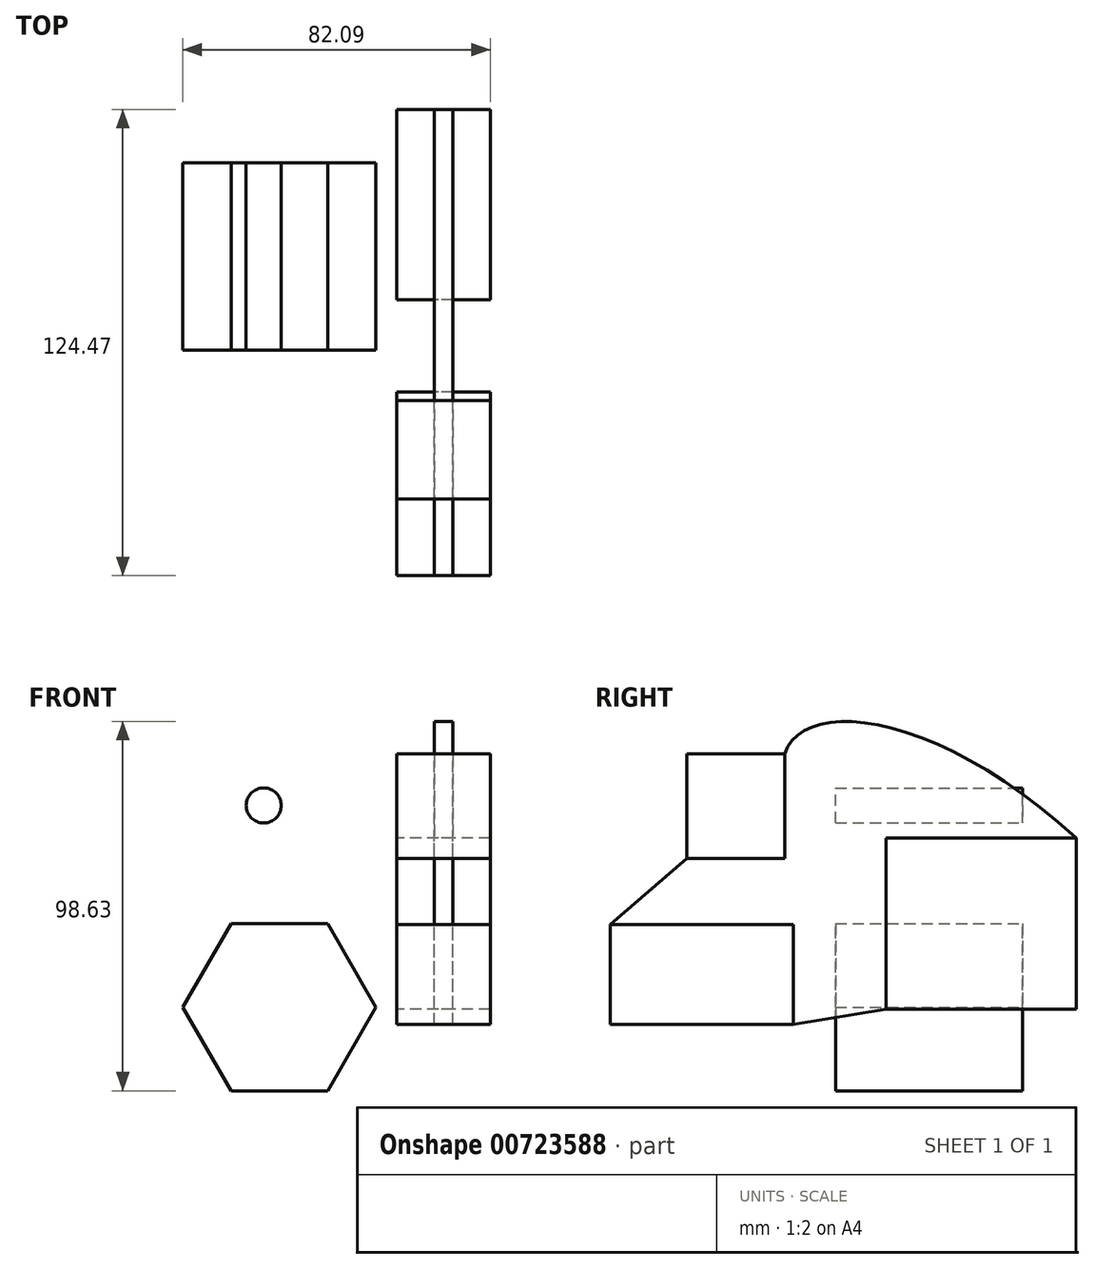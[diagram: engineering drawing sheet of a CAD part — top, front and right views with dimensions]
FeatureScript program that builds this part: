
annotation { "Feature Type Name" : "Feature", "Feature Type Description" : "" }
export const myFeature = defineFeature(function(context is Context, id is Id, definition is map)
    precondition{}
    {
        {
            var Q0;
            Q0=qCreatedBy(makeId("Right.planeOp"),FACE);
            var sketch = newSketch(context, id + "F0", { "sketchPlane" : qUnion([Q0])});
            skLineSegment(sketch, "E0.bottom", {"start": v(-64.75, 9.53) * mm, "end": v(-38.52, 9.53) * mm});
            skLineSegment(sketch, "E0.top", {"start": v(-64.75, 37.47) * mm, "end": v(-38.52, 37.47) * mm});
            skLineSegment(sketch, "E0.left", {"start": v(-64.75, 9.53) * mm, "end": v(-64.75, 37.47) * mm});
            skLineSegment(sketch, "E0.right", {"start": v(-38.52, 9.53) * mm, "end": v(-38.52, 37.47) * mm});
            skPoint(sketch, "E0.middle", {"position": v(-51.64, 23.5) * mm});
            skLineSegment(sketch, "E1.bottom", {"start": v(-36.2, -34.75) * mm, "end": v(-85.2, -34.75) * mm});
            skLineSegment(sketch, "E1.top", {"start": v(-36.2, -8.07) * mm, "end": v(-85.2, -8.07) * mm});
            skLineSegment(sketch, "E1.left", {"start": v(-36.2, -34.75) * mm, "end": v(-36.2, -8.07) * mm});
            skLineSegment(sketch, "E1.right", {"start": v(-85.2, -34.75) * mm, "end": v(-85.2, -8.07) * mm});
            skPoint(sketch, "E1.middle", {"position": v(-60.7, -21.41) * mm});
            skLineSegment(sketch, "E2.bottom", {"start": v(39.28, -30.76) * mm, "end": v(-11.52, -30.76) * mm});
            skLineSegment(sketch, "E2.top", {"start": v(39.28, 14.97) * mm, "end": v(-11.52, 14.97) * mm});
            skLineSegment(sketch, "E2.left", {"start": v(39.28, -30.76) * mm, "end": v(39.28, 14.97) * mm});
            skLineSegment(sketch, "E2.right", {"start": v(-11.52, -30.76) * mm, "end": v(-11.52, 14.97) * mm});
            skPoint(sketch, "E2.middle", {"position": v(13.88, -7.9) * mm});
            skLineSegment(sketch, "E3", {"start": v(-11.52, 14.97) * mm, "end": v(-38.52, 37.47) * mm});
            skLineSegment(sketch, "E4", {"start": v(-36.2, -34.75) * mm, "end": v(-11.52, -30.76) * mm});
            skLineSegment(sketch, "E5", {"start": v(-85.2, -8.07) * mm, "end": v(-64.75, 9.53) * mm});
            skFitSpline(sketch, "E6", {"points": [v(-38.52, 37.47) * mm, v(39.28, 14.97) * mm], "startDerivative": vector(14.54, 45.73) * mm, "endDerivative": vector(112.18, -102.88) * mm});
            skSolve(sketch);
        }
        {
            var Q0;
            Q0=makeQuery(id+"F0.imprint","IMPRINT",FACE,{"disambiguationData":[TD([[makeQuery(id+"F0.imprint","IMPRINT",EDGE,{"derivedFrom":sQuery(id+"F0.wireOp",EDGE,"E0.bottom")}),1.0]])]});
            var Q1;
            Q1=makeQuery(id+"F0.imprint","IMPRINT",FACE,{"disambiguationData":[TD([[makeQuery(id+"F0.imprint","IMPRINT",EDGE,{"derivedFrom":sQuery(id+"F0.wireOp",EDGE,"E2.bottom")}),-1.0]])]});
            var Q2;
            Q2=makeQuery(id+"F0.imprint","IMPRINT",FACE,{"disambiguationData":[TD([[makeQuery(id+"F0.imprint","IMPRINT",EDGE,{"derivedFrom":sQuery(id+"F0.wireOp",EDGE,"E1.bottom")}),-1.0]])]});
            extrude(context, id + "F1", {"entities" : qUnion([Q0, Q1, Q2]), "endBound" : BoundingType.SYMMETRIC, "depth" : 25 * mm, "offsetDistance" : 25 * mm});
        }
        {
            var Q0;
            Q0=makeQuery(id+"F0.imprint","IMPRINT",FACE,{"disambiguationData":[TD([[makeQuery(id+"F0.imprint","IMPRINT",EDGE,{"derivedFrom":sQuery(id+"F0.wireOp",EDGE,"E0.bottom")}),-1.0]])]});
            var Q1;
            Q1=makeQuery(id+"F0.imprint","IMPRINT",FACE,{"disambiguationData":[TD([[makeQuery(id+"F0.imprint","IMPRINT",EDGE,{"derivedFrom":sQuery(id+"F0.wireOp",EDGE,"E2.top")}),-1.0]])]});
            extrude(context, id + "F2", {"entities" : qUnion([Q0, Q1]), "endBound" : BoundingType.SYMMETRIC, "depth" : 5 * mm, "offsetDistance" : 25 * mm});
        }
        {
            var Q0;
            Q0=qCreatedBy(makeId("Front.planeOp"),FACE);
            var sketch = newSketch(context, id + "F3", { "sketchPlane" : qUnion([Q0])});
            skCircle(sketch, "E7", {"center": v(-48, 23.68) * mm, "radius": 4.68 * mm});
            skCircle(sketch, "E8.cCircle", {"center": v(-43.82, -30.21) * mm, "radius": 25.77 * mm, "construction": true});
            skLineSegment(sketch, "E8.0", {"start": v(-56.7, -52.53) * mm, "end": v(-69.6, -30.21) * mm});
            skLineSegment(sketch, "E8.1", {"start": v(-69.6, -30.21) * mm, "end": v(-56.7, -7.9) * mm});
            skLineSegment(sketch, "E8.2", {"start": v(-56.7, -7.9) * mm, "end": v(-30.94, -7.9) * mm});
            skLineSegment(sketch, "E8.3", {"start": v(-30.94, -7.9) * mm, "end": v(-18.05, -30.2) * mm});
            skLineSegment(sketch, "E8.4", {"start": v(-18.05, -30.2) * mm, "end": v(-30.93, -52.53) * mm});
            skLineSegment(sketch, "E8.5", {"start": v(-30.93, -52.53) * mm, "end": v(-56.7, -52.53) * mm});
            skSolve(sketch);
        }
        {
            var Q0;
            Q0=makeQuery(id+"F3.imprint","IMPRINT",FACE,{"disambiguationData":[TD([[makeQuery(id+"F3.imprint","IMPRINT",EDGE,{"derivedFrom":sQuery(id+"F3.wireOp",EDGE,"E7")}),1.0]])]});
            var Q1;
            Q1=makeQuery(id+"F3.imprint","IMPRINT",FACE,{"disambiguationData":[TD([[makeQuery(id+"F3.imprint","IMPRINT",EDGE,{"derivedFrom":sQuery(id+"F3.wireOp",EDGE,"E8.0")}),-1.0]])]});
            extrude(context, id + "F4", {"entities" : qUnion([Q0, Q1]), "endBound" : BoundingType.SYMMETRIC, "depth" : 50 * mm, "offsetDistance" : 25 * mm});
        }
    });
